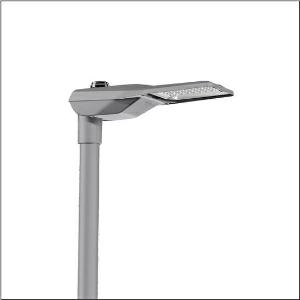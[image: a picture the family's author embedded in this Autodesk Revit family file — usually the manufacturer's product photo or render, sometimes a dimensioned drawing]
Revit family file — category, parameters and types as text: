
# Revit family: streetlight_sl_21_mini___st0_5a_5xe6b37n08hb_16a2
name_source: partatom
category: Lighting Fixtures
units: mm (PartAtom-declared; Revit-internal decimal feet)

## family parameters
Cut with Voids When Loaded = No
Host = Face
Light Source = No
Part Type = Normal
Room Calculation Point = No
Round Connector Dimension = Use Diameter
Shared = No

## types (1)
- --- (1 x LED, 9040 lm, 66 W, 3000K)
    Apparent Load = 66 VA
    CIE Flux Codes = 41 75 97 100 100
    Color Rendering = 70
    Color Temperature = 3000K
    Default Elevation = 1800 mm
    Description = Streetlight SL 21 mini, mast luminaire, primary light control with lens, of PMMA, primary optical cover: cover, of toughened safety glass, transparent, light distribution: ST0.5a, light emission: direct distribution, primary light characteristic: asymmetric, installation type: side-entry, LED, 3G 1.5mm², High Power LED, rated luminous flux: 9.040lm, luminous efficacy: 137lm/W, light colour: 730, colour temperature: 3000K, control gear: NEMA (7pin), control: overheat protection, pre-setting: linear dimming characteristic, constant luminous flux control, time-dependent luminous flux control, flexible luminous flux parameterisation, mains connection: 230..240V, AC, 50/60Hz, connection cable pre-assembled, cable length: 8,5m, wiring characteristics: H07RN-F, start of lifetime: 66W, end of service life: 69W, reduction: 30W, luminaire housing, of diecast aluminium (EN AC-44300), powder-coated, SITECO metallic grey (DB 702S), corrosivity category C5 high according to DIN EN ISO 12944, multi-level sealing system, sealing non-destructively replaceable, inclination adjustable: 0°, 5°, 10°, 15°, length: 628mm, width: 235mm, height: 110mm, spigot size: 42mm (side-entry), mounting height: 4..8m, protection rating (complete): IP66, insulation class (complete): insulation class I (protective earthing), certification: CE, ENEC, ENEC+, VDE, impact resistance: IK10, permissible operating ambient temperature for outdoor applications: -40..+50°C, standard-compliant lighting for roads and squares, packaging unit: 1 piece

Light Distribution: ST0.5a
    Height = 110 mm
    Lamp = 1 x LED
    Lamp Light Flux = 9040 lm
    Lamp Power = 66 W
    Lamp count = 1
    Length = 625 mm
    Luminous efficacy = 137 lm/W
    Manufacturer = Siteco
    ModVariant = No
    Model = 5XE6B37N08HB
    Mounting Place = Pole
    Mounting Type = Pole top
    Number of Poles = 1
    OnlyDefault = Yes
    Power Factor = 1
    Product Name = Streetlight SL 21 mini | ST0.5a
    Product group = mast luminaire | pylon top
    ProductGroupID = 6100
    Protection Class = Protection class I
    Protection Degree = IP 66
    RLX_Detail_Level = 1
    RLX_Emergency_Light_Flux = 0 lm
    RLX_Emergency_Type = 0
    RLX_Emergency_Type_DB = No
    RlxData = <blob elided: 37177 chars, md5=0190f4bf>
    Socket = socket
    Standby Power = 0 W
    System Light Flux = 9040 lm
    System Power = 66 W
    Type Comments = factory setting: luminous flux: 100 % | dim-lin: 254 | 670 mA
    Type Image = l_1294379.jpg
    URL = http://relux.com
    VarID = @adj_138547
    Voltage = 0 V
    Weight = 0.00 kg
    Width = 234 mm

## geometry (parser evidence)
native form markers: Blend x4, Sweep x9
no freeform markers — native parametric forms only
